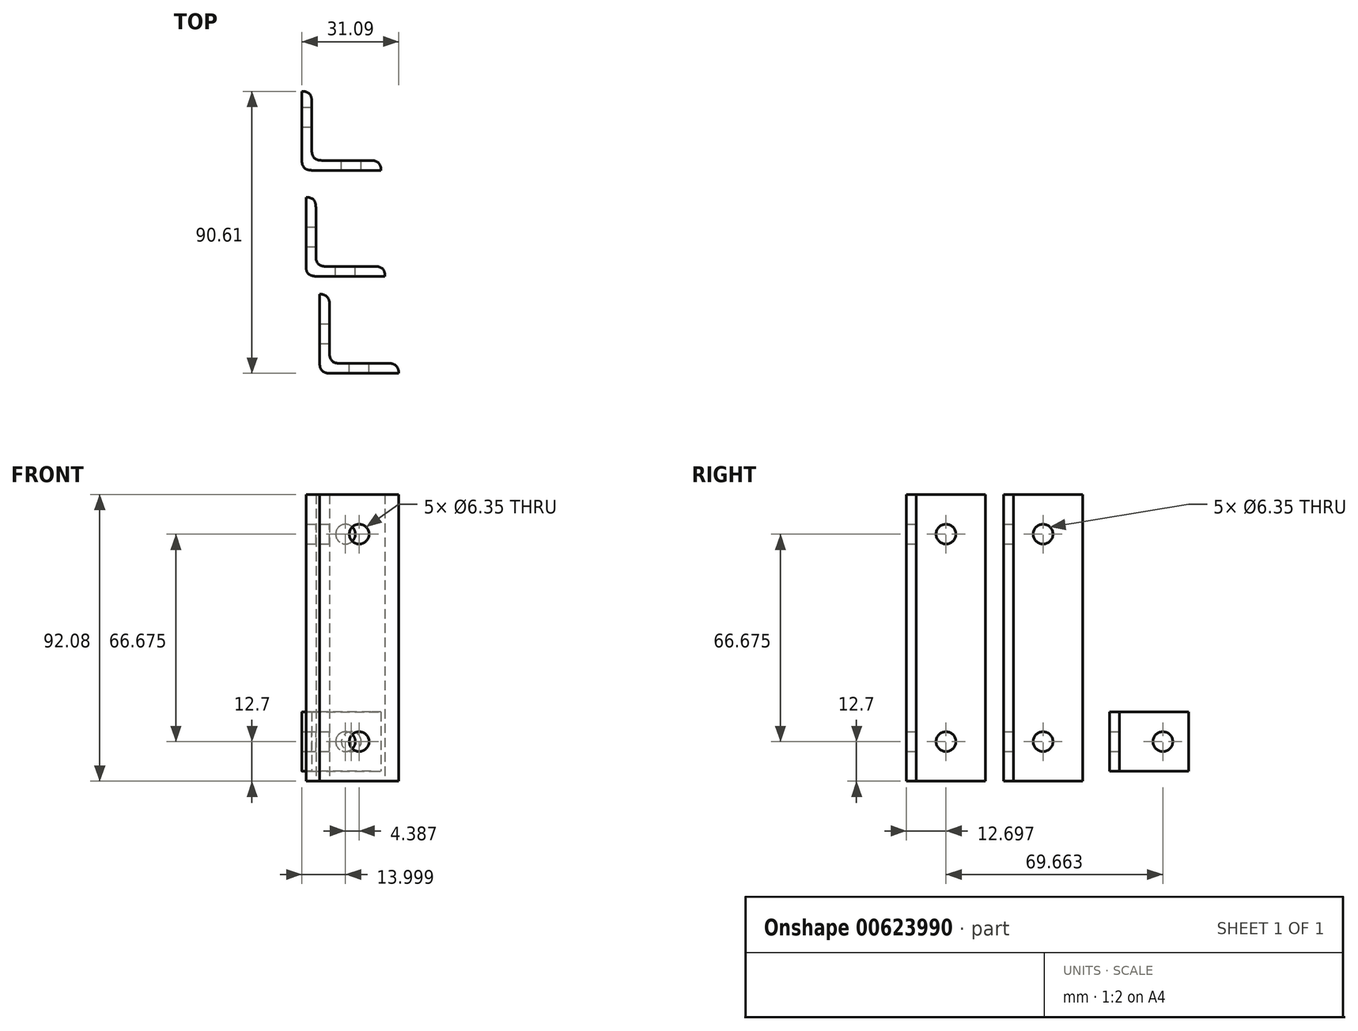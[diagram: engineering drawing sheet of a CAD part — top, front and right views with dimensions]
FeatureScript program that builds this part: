
annotation { "Feature Type Name" : "Feature", "Feature Type Description" : "" }
export const myFeature = defineFeature(function(context is Context, id is Id, definition is map)
    precondition{}
    {
        {
            var Q0;
            Q0=qCreatedBy(makeId("Top.planeOp"),FACE);
            var sketch = newSketch(context, id + "F0", { "sketchPlane" : qUnion([Q0])});
            skLineSegment(sketch, "E0", {"start": v(-38.51, 29.2) * mm, "end": v(-38.51, 3.8) * mm});
            skLineSegment(sketch, "E1", {"start": v(-38.51, 3.8) * mm, "end": v(-13.11, 3.8) * mm});
            skLineSegment(sketch, "E2", {"start": v(-13.11, 3.8) * mm, "end": v(-13.11, 6.98) * mm});
            skLineSegment(sketch, "E3", {"start": v(-13.11, 6.98) * mm, "end": v(-35.34, 6.98) * mm});
            skLineSegment(sketch, "E4", {"start": v(-35.34, 6.98) * mm, "end": v(-35.34, 29.2) * mm});
            skLineSegment(sketch, "E5", {"start": v(-35.34, 29.2) * mm, "end": v(-38.51, 29.2) * mm});
            skLineSegment(sketch, "E6", {"start": v(4.34, 3.8) * mm, "end": v(29.74, 3.8) * mm});
            skLineSegment(sketch, "E7", {"start": v(29.74, 3.8) * mm, "end": v(29.74, 6.98) * mm});
            skLineSegment(sketch, "E8", {"start": v(29.74, 6.98) * mm, "end": v(7.52, 6.98) * mm});
            skLineSegment(sketch, "E9", {"start": v(7.52, 6.98) * mm, "end": v(7.52, 29.2) * mm});
            skLineSegment(sketch, "E10", {"start": v(7.52, 29.2) * mm, "end": v(4.34, 29.2) * mm});
            skLineSegment(sketch, "E11", {"start": v(4.34, 29.2) * mm, "end": v(4.34, 3.8) * mm});
            skSolve(sketch);
        }
        {
            var Q0;
            Q0=makeQuery(id+"F0.imprint","IMPRINT",FACE,{"disambiguationData":[TD([[makeQuery(id+"F0.imprint","IMPRINT",EDGE,{"derivedFrom":sQuery(id+"F0.wireOp",EDGE,"E0")}),1.0]])]});
            extrude(context, id + "F1", {"entities" : qUnion([Q0]), "depth" : 25.4 * mm, "offsetDistance" : 25.4 * mm});
        }
        {
            var Q0;
            Q0=qCreatedBy(makeId("Top.planeOp"),FACE);
            var sketch = newSketch(context, id + "F2", { "sketchPlane" : qUnion([Q0])});
            skLineSegment(sketch, "E12", {"start": v(-37.21, -30.25) * mm, "end": v(-37.21, -4.85) * mm});
            skLineSegment(sketch, "E13", {"start": v(-37.21, -4.85) * mm, "end": v(-34.04, -4.85) * mm});
            skLineSegment(sketch, "E14", {"start": v(-34.04, -4.85) * mm, "end": v(-34.04, -27.07) * mm});
            skLineSegment(sketch, "E15", {"start": v(-34.04, -27.07) * mm, "end": v(-11.81, -27.07) * mm});
            skLineSegment(sketch, "E16", {"start": v(-11.81, -27.07) * mm, "end": v(-11.81, -30.25) * mm});
            skLineSegment(sketch, "E17", {"start": v(-11.81, -30.25) * mm, "end": v(-37.21, -30.25) * mm});
            skLineSegment(sketch, "E18", {"start": v(-7.42, -30.25) * mm, "end": v(17.98, -30.25) * mm});
            skLineSegment(sketch, "E19", {"start": v(17.98, -30.25) * mm, "end": v(17.98, -27.07) * mm});
            skLineSegment(sketch, "E20", {"start": v(17.98, -27.07) * mm, "end": v(-4.25, -27.07) * mm});
            skLineSegment(sketch, "E21", {"start": v(-4.25, -27.07) * mm, "end": v(-4.25, -4.85) * mm});
            skLineSegment(sketch, "E22", {"start": v(-4.25, -4.85) * mm, "end": v(-7.42, -4.85) * mm});
            skLineSegment(sketch, "E23", {"start": v(-7.42, -4.85) * mm, "end": v(-7.42, -30.25) * mm});
            skLineSegment(sketch, "E24", {"start": v(-32.82, -61.41) * mm, "end": v(-32.82, -36.01) * mm});
            skLineSegment(sketch, "E25", {"start": v(-32.82, -36.01) * mm, "end": v(-29.65, -36.01) * mm});
            skLineSegment(sketch, "E26", {"start": v(-29.65, -36.01) * mm, "end": v(-29.65, -58.24) * mm});
            skLineSegment(sketch, "E27", {"start": v(-29.65, -58.24) * mm, "end": v(-7.42, -58.24) * mm});
            skLineSegment(sketch, "E28", {"start": v(-7.42, -58.24) * mm, "end": v(-7.42, -61.41) * mm});
            skLineSegment(sketch, "E29", {"start": v(-7.42, -61.41) * mm, "end": v(-32.82, -61.41) * mm});
            skSolve(sketch);
        }
        {
            var Q0;
            Q0=makeQuery(id+"F0.imprint","IMPRINT",FACE,{"disambiguationData":[TD([[makeQuery(id+"F0.imprint","IMPRINT",EDGE,{"derivedFrom":sQuery(id+"F0.wireOp",EDGE,"E6")}),1.0]])]});
            var Q1;
            Q1=makeQuery(id+"F2.imprint","IMPRINT",FACE,{"disambiguationData":[TD([[makeQuery(id+"F2.imprint","IMPRINT",EDGE,{"derivedFrom":sQuery(id+"F2.wireOp",EDGE,"E12")}),-1.0]])]});
            var Q2;
            Q2=makeQuery(id+"F2.imprint","IMPRINT",FACE,{"disambiguationData":[TD([[makeQuery(id+"F2.imprint","IMPRINT",EDGE,{"derivedFrom":sQuery(id+"F2.wireOp",EDGE,"E18")}),1.0]])]});
            var Q3;
            Q3=makeQuery(id+"F2.imprint","IMPRINT",FACE,{"disambiguationData":[TD([[makeQuery(id+"F2.imprint","IMPRINT",EDGE,{"derivedFrom":sQuery(id+"F2.wireOp",EDGE,"E24")}),-1.0]])]});
            extrude(context, id + "F3", {"entities" : qUnion([Q0, Q1, Q2, Q3]), "depth" : 92.07 * mm, "offsetDistance" : 25.4 * mm});
        }
        {
            var Q0;
            Q0=makeQuery(id+"F3.opExtrude","SWEPT_BODY",BODY,{"disambiguationData":[OSD([sQuery(id+"F0.wireOp",EDGE,"E6"),sQuery(id+"F0.wireOp",EDGE,"E7"),sQuery(id+"F0.wireOp",EDGE,"E8"),sQuery(id+"F0.wireOp",EDGE,"E9"),sQuery(id+"F0.wireOp",EDGE,"E10"),sQuery(id+"F0.wireOp",EDGE,"E11")])]});
            deleteBodies(context, id + "F4", {"entities" : qUnion([Q0])});
        }
        {
            var Q0;
            Q0=makeQuery(id+"F3.opExtrude","SWEPT_BODY",BODY,{"disambiguationData":[OSD([sQuery(id+"F2.wireOp",EDGE,"E18"),sQuery(id+"F2.wireOp",EDGE,"E19"),sQuery(id+"F2.wireOp",EDGE,"E20"),sQuery(id+"F2.wireOp",EDGE,"E21"),sQuery(id+"F2.wireOp",EDGE,"E22"),sQuery(id+"F2.wireOp",EDGE,"E23")])]});
            deleteBodies(context, id + "F5", {"entities" : qUnion([Q0])});
        }
        {
            var Q0;
            Q0=makeQuery(id+"F1.opExtrude","SWEPT_FACE",FACE,{"disambiguationData":[OSD([sQuery(id+"F0.wireOp",EDGE,"E4")])]});
            var sketch = newSketch(context, id + "F6", { "sketchPlane" : qUnion([Q0])});
            skCircle(sketch, "E30", {"center": v(20.95, 12.7) * mm, "radius": 3.18 * mm});
            skPoint(sketch, "E30.centerSnap0", {"position": v(20.95, 25.4) * mm});
            skPoint(sketch, "E30.centerSnap1", {"position": v(29.2, 12.7) * mm});
            skSolve(sketch);
        }
        {
            var Q0;
            Q0=makeQuery(id+"F3.opExtrude","SWEPT_FACE",FACE,{"disambiguationData":[OSD([sQuery(id+"F2.wireOp",EDGE,"E27")])]});
            var sketch = newSketch(context, id + "F7", { "sketchPlane" : qUnion([Q0])});
            skCircle(sketch, "E31", {"center": v(20.12, 79.38) * mm, "radius": 3.18 * mm});
            skCircle(sketch, "E32", {"center": v(20.12, 12.7) * mm, "radius": 3.18 * mm});
            skSolve(sketch);
        }
        {
            var Q0;
            Q0=makeQuery(id+"F3.opExtrude","SWEPT_FACE",FACE,{"disambiguationData":[OSD([sQuery(id+"F2.wireOp",EDGE,"E15")])]});
            var sketch = newSketch(context, id + "F8", { "sketchPlane" : qUnion([Q0])});
            skCircle(sketch, "E33", {"center": v(24.51, 79.38) * mm, "radius": 3.18 * mm});
            skCircle(sketch, "E34", {"center": v(24.51, 12.7) * mm, "radius": 3.18 * mm});
            skPoint(sketch, "E34.perimeterSnap0", {"position": v(22.92, 0) * mm});
            skSolve(sketch);
        }
        {
            var Q0;
            Q0=makeQuery(id+"F7.imprint","IMPRINT",FACE,{"disambiguationData":[TD([[makeQuery(id+"F7.imprint","IMPRINT",EDGE,{"derivedFrom":sQuery(id+"F7.wireOp",EDGE,"E31")}),1.0]])]});
            var Q1;
            Q1=makeQuery(id+"F7.imprint","IMPRINT",FACE,{"disambiguationData":[TD([[makeQuery(id+"F7.imprint","IMPRINT",EDGE,{"derivedFrom":sQuery(id+"F7.wireOp",EDGE,"E32")}),1.0]])]});
            extrude(context, id + "F9", {"entities" : qUnion([Q0, Q1]), "operationType" : NewBodyOperationType.REMOVE, "oppositeDirection" : true, "depth" : 3.17 * mm, "offsetDistance" : 25.4 * mm});
        }
        {
            var Q0;
            Q0=makeQuery(id+"F8.imprint","IMPRINT",FACE,{"disambiguationData":[TD([[makeQuery(id+"F8.imprint","IMPRINT",EDGE,{"derivedFrom":sQuery(id+"F8.wireOp",EDGE,"E33")}),1.0]])]});
            var Q1;
            Q1=makeQuery(id+"F8.imprint","IMPRINT",FACE,{"disambiguationData":[TD([[makeQuery(id+"F8.imprint","IMPRINT",EDGE,{"derivedFrom":sQuery(id+"F8.wireOp",EDGE,"E34")}),1.0]])]});
            extrude(context, id + "F10", {"entities" : qUnion([Q0, Q1]), "operationType" : NewBodyOperationType.REMOVE, "oppositeDirection" : true, "depth" : 3.17 * mm, "offsetDistance" : 25.4 * mm});
        }
        {
            var Q0;
            Q0=makeQuery(id+"F3.opExtrude","SWEPT_FACE",FACE,{"disambiguationData":[OSD([sQuery(id+"F2.wireOp",EDGE,"E26")])]});
            var sketch = newSketch(context, id + "F11", { "sketchPlane" : qUnion([Q0])});
            skCircle(sketch, "E35", {"center": v(-48.71, 79.38) * mm, "radius": 3.18 * mm});
            skCircle(sketch, "E36", {"center": v(-48.71, 12.7) * mm, "radius": 3.18 * mm});
            skSolve(sketch);
        }
        {
            var Q0;
            Q0=makeQuery(id+"F3.opExtrude","SWEPT_FACE",FACE,{"disambiguationData":[OSD([sQuery(id+"F2.wireOp",EDGE,"E14")])]});
            var sketch = newSketch(context, id + "F12", { "sketchPlane" : qUnion([Q0])});
            skCircle(sketch, "E37", {"center": v(-17.55, 79.38) * mm, "radius": 3.18 * mm});
            skCircle(sketch, "E38", {"center": v(-17.55, 12.7) * mm, "radius": 3.18 * mm});
            skSolve(sketch);
        }
        {
            var Q0;
            Q0=makeQuery(id+"F11.imprint","IMPRINT",FACE,{"disambiguationData":[TD([[makeQuery(id+"F11.imprint","IMPRINT",EDGE,{"derivedFrom":sQuery(id+"F11.wireOp",EDGE,"E35")}),1.0]])]});
            var Q1;
            Q1=makeQuery(id+"F11.imprint","IMPRINT",FACE,{"disambiguationData":[TD([[makeQuery(id+"F11.imprint","IMPRINT",EDGE,{"derivedFrom":sQuery(id+"F11.wireOp",EDGE,"E36")}),1.0]])]});
            extrude(context, id + "F13", {"entities" : qUnion([Q0, Q1]), "operationType" : NewBodyOperationType.REMOVE, "oppositeDirection" : true, "depth" : 3.17 * mm, "offsetDistance" : 25.4 * mm});
        }
        {
            var Q0;
            Q0=makeQuery(id+"F12.imprint","IMPRINT",FACE,{"disambiguationData":[TD([[makeQuery(id+"F12.imprint","IMPRINT",EDGE,{"derivedFrom":sQuery(id+"F12.wireOp",EDGE,"E37")}),1.0]])]});
            var Q1;
            Q1=makeQuery(id+"F12.imprint","IMPRINT",FACE,{"disambiguationData":[TD([[makeQuery(id+"F12.imprint","IMPRINT",EDGE,{"derivedFrom":sQuery(id+"F12.wireOp",EDGE,"E38")}),1.0]])]});
            extrude(context, id + "F14", {"entities" : qUnion([Q0, Q1]), "operationType" : NewBodyOperationType.REMOVE, "oppositeDirection" : true, "depth" : 3.17 * mm, "offsetDistance" : 25.4 * mm});
        }
        {
            var Q0;
            Q0=makeQuery(id+"F6.imprint","IMPRINT",FACE,{"disambiguationData":[TD([[makeQuery(id+"F6.imprint","IMPRINT",EDGE,{"derivedFrom":sQuery(id+"F6.wireOp",EDGE,"E30")}),1.0]])]});
            extrude(context, id + "F15", {"entities" : qUnion([Q0]), "operationType" : NewBodyOperationType.REMOVE, "oppositeDirection" : true, "depth" : 3.17 * mm, "offsetDistance" : 25.4 * mm});
        }
        {
            var Q0;
            Q0=makeQuery(id+"F1.opExtrude","SWEPT_FACE",FACE,{"disambiguationData":[OSD([sQuery(id+"F0.wireOp",EDGE,"E3")])]});
            var sketch = newSketch(context, id + "F16", { "sketchPlane" : qUnion([Q0])});
            skCircle(sketch, "E39", {"center": v(22.64, 12.7) * mm, "radius": 3.18 * mm});
            skPoint(sketch, "E39.centerSnap0", {"position": v(13.11, 12.7) * mm});
            skSolve(sketch);
        }
        {
            var Q0;
            Q0=makeQuery(id+"F16.imprint","IMPRINT",FACE,{"disambiguationData":[TD([[makeQuery(id+"F16.imprint","IMPRINT",EDGE,{"derivedFrom":sQuery(id+"F16.wireOp",EDGE,"E39")}),1.0]])]});
            extrude(context, id + "F17", {"entities" : qUnion([Q0]), "operationType" : NewBodyOperationType.REMOVE, "oppositeDirection" : true, "depth" : 3.17 * mm, "offsetDistance" : 25.4 * mm});
        }
        {
            var Q0;
            Q0=makeQuery(id+"F3.opExtrude","SWEPT_EDGE",EDGE,{"disambiguationData":[OSD([sQuery(id+"F2.wireOp",EDGE,"E14"),sQuery(id+"F2.wireOp",EDGE,"E15")])]});
            var Q1;
            Q1=makeQuery(id+"F1.opExtrude","SWEPT_EDGE",EDGE,{"disambiguationData":[OSD([sQuery(id+"F0.wireOp",EDGE,"E3"),sQuery(id+"F0.wireOp",EDGE,"E4")])]});
            var Q2;
            Q2=makeQuery(id+"F3.opExtrude","SWEPT_EDGE",EDGE,{"disambiguationData":[OSD([sQuery(id+"F2.wireOp",EDGE,"E26"),sQuery(id+"F2.wireOp",EDGE,"E27")])]});
            var Q3;
            Q3=makeQuery(id+"F1.opExtrude","SWEPT_EDGE",EDGE,{"disambiguationData":[OSD([sQuery(id+"F0.wireOp",EDGE,"E0"),sQuery(id+"F0.wireOp",EDGE,"E1")])]});
            var Q4;
            Q4=makeQuery(id+"F3.opExtrude","SWEPT_EDGE",EDGE,{"disambiguationData":[OSD([sQuery(id+"F2.wireOp",EDGE,"E12"),sQuery(id+"F2.wireOp",EDGE,"E17")])]});
            var Q5;
            Q5=makeQuery(id+"F3.opExtrude","SWEPT_EDGE",EDGE,{"disambiguationData":[OSD([sQuery(id+"F2.wireOp",EDGE,"E24"),sQuery(id+"F2.wireOp",EDGE,"E29")])]});
            var Q6;
            Q6=makeQuery(id+"F3.opExtrude","SWEPT_EDGE",EDGE,{"disambiguationData":[OSD([sQuery(id+"F2.wireOp",EDGE,"E27"),sQuery(id+"F2.wireOp",EDGE,"E28")])]});
            var Q7;
            Q7=makeQuery(id+"F3.opExtrude","SWEPT_EDGE",EDGE,{"disambiguationData":[OSD([sQuery(id+"F2.wireOp",EDGE,"E15"),sQuery(id+"F2.wireOp",EDGE,"E16")])]});
            var Q8;
            Q8=makeQuery(id+"F1.opExtrude","SWEPT_EDGE",EDGE,{"disambiguationData":[OSD([sQuery(id+"F0.wireOp",EDGE,"E2"),sQuery(id+"F0.wireOp",EDGE,"E3")])]});
            var Q9;
            Q9=makeQuery(id+"F1.opExtrude","SWEPT_EDGE",EDGE,{"disambiguationData":[OSD([sQuery(id+"F0.wireOp",EDGE,"E4"),sQuery(id+"F0.wireOp",EDGE,"E5")])]});
            var Q10;
            Q10=makeQuery(id+"F3.opExtrude","SWEPT_EDGE",EDGE,{"disambiguationData":[OSD([sQuery(id+"F2.wireOp",EDGE,"E25"),sQuery(id+"F2.wireOp",EDGE,"E26")])]});
            var Q11;
            Q11=makeQuery(id+"F3.opExtrude","SWEPT_EDGE",EDGE,{"disambiguationData":[OSD([sQuery(id+"F2.wireOp",EDGE,"E13"),sQuery(id+"F2.wireOp",EDGE,"E14")])]});
            fillet(context, id + "F18", {"entities" : qUnion([Q0, Q1, Q2, Q3, Q4, Q5, Q6, Q7, Q8, Q9, Q10, Q11]), "radius" : 3.17 * mm, "tangentPropagation" : true, "rho" : 0.5, "crossSection" : FilletCrossSection.CONIC, "allowEdgeOverflow" : false});
        }
        {
            var Q0;
            Q0=makeQuery(id+"F1.opExtrude","CAP_FACE",FACE,{"disambiguationData":[OSD([sQuery(id+"F0.wireOp",EDGE,"E0"),sQuery(id+"F0.wireOp",EDGE,"E1"),sQuery(id+"F0.wireOp",EDGE,"E2"),sQuery(id+"F0.wireOp",EDGE,"E3"),sQuery(id+"F0.wireOp",EDGE,"E4"),sQuery(id+"F0.wireOp",EDGE,"E5")])],"isStart":true});
            extrude(context, id + "F19", {"entities" : qUnion([Q0]), "operationType" : NewBodyOperationType.REMOVE, "oppositeDirection" : true, "depth" : 1.59 * mm, "offsetDistance" : 25.4 * mm});
        }
        {
            var Q0;
            Q0=makeQuery(id+"F1.opExtrude","CAP_FACE",FACE,{"disambiguationData":[OSD([sQuery(id+"F0.wireOp",EDGE,"E0"),sQuery(id+"F0.wireOp",EDGE,"E1"),sQuery(id+"F0.wireOp",EDGE,"E2"),sQuery(id+"F0.wireOp",EDGE,"E3"),sQuery(id+"F0.wireOp",EDGE,"E4"),sQuery(id+"F0.wireOp",EDGE,"E5")])],"isStart":false});
            extrude(context, id + "F20", {"entities" : qUnion([Q0]), "operationType" : NewBodyOperationType.REMOVE, "oppositeDirection" : true, "depth" : 1.59 * mm, "offsetDistance" : 25.4 * mm});
        }
        {
            var Q0;
            Q0=makeQuery(id+"F19.boolean.opBoolean","COPY",FACE,{"derivedFrom":makeQuery(id+"F19.opExtrude","CAP_FACE",FACE,{"disambiguationData":[OSD([sQuery(id+"F0.wireOp",EDGE,"E0"),sQuery(id+"F0.wireOp",EDGE,"E1"),sQuery(id+"F0.wireOp",EDGE,"E2"),sQuery(id+"F0.wireOp",EDGE,"E3"),sQuery(id+"F0.wireOp",EDGE,"E4"),sQuery(id+"F0.wireOp",EDGE,"E5")])],"isStart":false})});
            extrude(context, id + "F21", {"entities" : qUnion([Q0]), "operationType" : NewBodyOperationType.REMOVE, "oppositeDirection" : true, "depth" : 1.59 * mm, "offsetDistance" : 25.4 * mm});
        }
        {
            var Q0;
            Q0=makeQuery(id+"F20.boolean.opBoolean","COPY",FACE,{"derivedFrom":makeQuery(id+"F20.opExtrude","CAP_FACE",FACE,{"disambiguationData":[OSD([sQuery(id+"F0.wireOp",EDGE,"E0"),sQuery(id+"F0.wireOp",EDGE,"E1"),sQuery(id+"F0.wireOp",EDGE,"E2"),sQuery(id+"F0.wireOp",EDGE,"E3"),sQuery(id+"F0.wireOp",EDGE,"E4"),sQuery(id+"F0.wireOp",EDGE,"E5")])],"isStart":false})});
            extrude(context, id + "F22", {"entities" : qUnion([Q0]), "operationType" : NewBodyOperationType.REMOVE, "oppositeDirection" : true, "depth" : 1.59 * mm, "offsetDistance" : 25.4 * mm});
        }
    });
